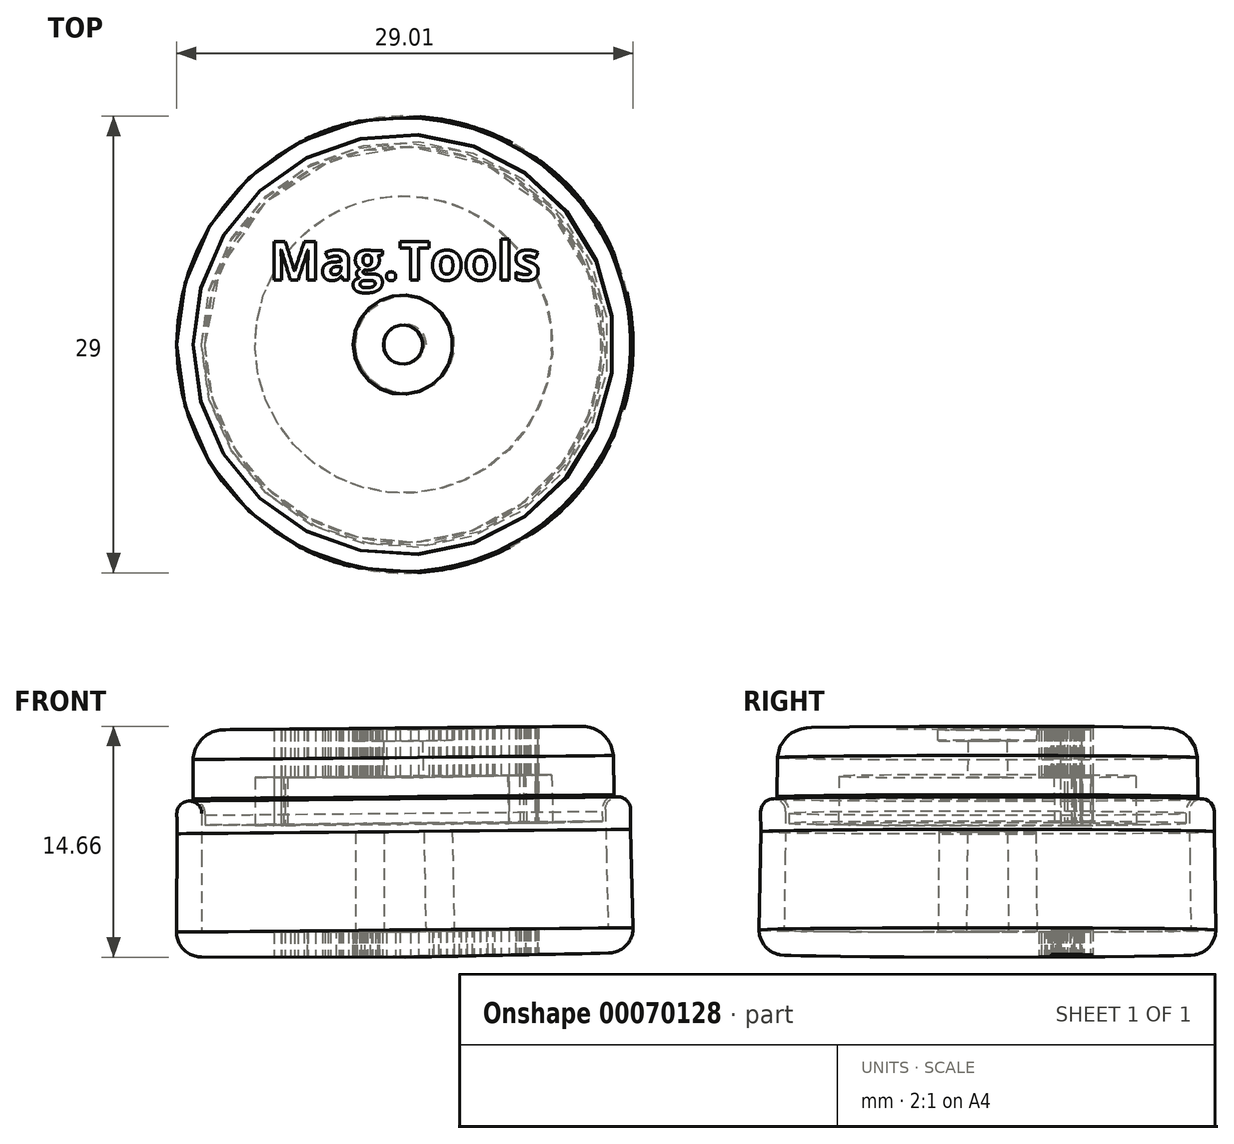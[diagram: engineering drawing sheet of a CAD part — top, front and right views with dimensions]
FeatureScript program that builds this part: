
annotation { "Feature Type Name" : "Feature", "Feature Type Description" : "" }
export const myFeature = defineFeature(function(context is Context, id is Id, definition is map)
    precondition{}
    {
        {
            var Q0;
            Q0=qCreatedBy(makeId("Front.planeOp"),FACE);
            var sketch = newSketch(context, id + "F0", { "sketchPlane" : qUnion([Q0])});
            skLineSegment(sketch, "E0", {"start": v(-3.15, 7.94) * mm, "end": v(-3.15, 1.6) * mm});
            skLineSegment(sketch, "E1", {"start": v(-1.35, 7.95) * mm, "end": v(-1.35, 1.6) * mm});
            skLineSegment(sketch, "E2", {"start": v(-1.35, 7.95) * mm, "end": v(-3.15, 7.94) * mm});
            skLineSegment(sketch, "E3", {"start": v(-12.9, 9.13) * mm, "end": v(-12.9, 6.49) * mm});
            skLineSegment(sketch, "E4", {"start": v(-12.9, 6.49) * mm, "end": v(-12.93, 1.6) * mm});
            skLineSegment(sketch, "E5", {"start": v(-14.5, 9.11) * mm, "end": v(-14.47, 7.84) * mm});
            skLineSegment(sketch, "E6", {"start": v(-14.47, 7.84) * mm, "end": v(-14.52, 1.6) * mm});
            skLineSegment(sketch, "E7", {"start": v(0, 0) * mm, "end": v(-12.93, 0.01) * mm});
            skLineSegment(sketch, "E8", {"start": v(-3.15, 1.6) * mm, "end": v(-12.93, 1.6) * mm});
            skLineSegment(sketch, "E9", {"start": v(-0.02, 1.6) * mm, "end": v(-1.35, 1.6) * mm});
            skLineSegment(sketch, "E10", {"start": v(0, 0) * mm, "end": v(-0.02, 1.6) * mm});
            skArc(sketch, "E11", {"start": v(-12.9, 9.13) * mm, "mid": v(-13.7, 9.92) * mm, "end": v(-14.5, 9.11) * mm});
            skArc(sketch, "E12", {"start": v(-14.52, 1.6) * mm, "mid": v(-14.05, 0.47) * mm, "end": v(-12.93, 0.01) * mm});
            skSolve(sketch);
        }
        {
            var Q0;
            Q0=qCreatedBy(makeId("Front.planeOp"),FACE);
            var sketch = newSketch(context, id + "F1", { "sketchPlane" : qUnion([Q0])});
            skLineSegment(sketch, "E13", {"start": v(-9.54, 8.36) * mm, "end": v(-12.7, 8.39) * mm});
            skLineSegment(sketch, "E14", {"start": v(-12.7, 8.39) * mm, "end": v(-12.7, 9.02) * mm});
            skLineSegment(sketch, "E15", {"start": v(-9.54, 11.4) * mm, "end": v(-9.54, 8.36) * mm});
            skLineSegment(sketch, "E16", {"start": v(-9.54, 11.4) * mm, "end": v(-1.37, 11.4) * mm});
            skLineSegment(sketch, "E17", {"start": v(-13.47, 12.55) * mm, "end": v(-13.47, 10.06) * mm});
            skArc(sketch, "E18", {"start": v(-12.7, 9.02) * mm, "mid": v(-12.9, 9.68) * mm, "end": v(-13.47, 10.06) * mm});
            skArc(sketch, "E19", {"start": v(-11.47, 14.45) * mm, "mid": v(-12.85, 13.9) * mm, "end": v(-13.47, 12.55) * mm});
            skLineSegment(sketch, "E20", {"start": v(-1.37, 11.4) * mm, "end": v(-1.37, 13.73) * mm});
            skLineSegment(sketch, "E21", {"start": v(-11.47, 14.45) * mm, "end": v(-3.3, 14.44) * mm});
            skLineSegment(sketch, "E22", {"start": v(-3.3, 14.44) * mm, "end": v(-3.27, 13.73) * mm});
            skLineSegment(sketch, "E23", {"start": v(-3.27, 13.73) * mm, "end": v(-1.37, 13.73) * mm});
            skSolve(sketch);
        }
        {
            var Q0;
            Q0=qSketchRegion(id+"F0",true);
            var Q1;
            Q1=sQuery(id+"F0.wireOp",EDGE,"E10");
            revolve(context, id + "F2", {"entities" : qUnion([Q0]), "axis" : qUnion([Q1]), "revolveType" : RevolveType.FULL});
        }
        {
            var Q0;
            Q0=qSketchRegion(id+"F1",true);
            var Q1;
            Q1=sQuery(id+"F0.wireOp",EDGE,"E10");
            revolve(context, id + "F3", {"entities" : qUnion([Q0]), "axis" : qUnion([Q1]), "revolveType" : RevolveType.FULL});
        }
        {
            var Q0;
            Q0=qCreatedBy(makeId("Top.planeOp"),FACE);
            var sketch = newSketch(context, id + "F4", { "sketchPlane" : qUnion([Q0])});
            skText(sketch, "E24", { "text": "Mag.Tools", "fontName": "OpenSans-Bold.ttf"});
            const initialGuessF4  = {"E24": [-0.00862, 0.0041, 1, 0, 0.00247]};
            skSetInitialGuess(sketch, initialGuessF4);
            skSolve(sketch);
        }
        {
            var Q0;
            Q0 = qSketchRegion(id + "F4", true);
            extrude(context, id + "F5", {"entities" : qUnion([Q0]), "operationType" : NewBodyOperationType.REMOVE, "depth" : 15 * mm});
        }
    });
